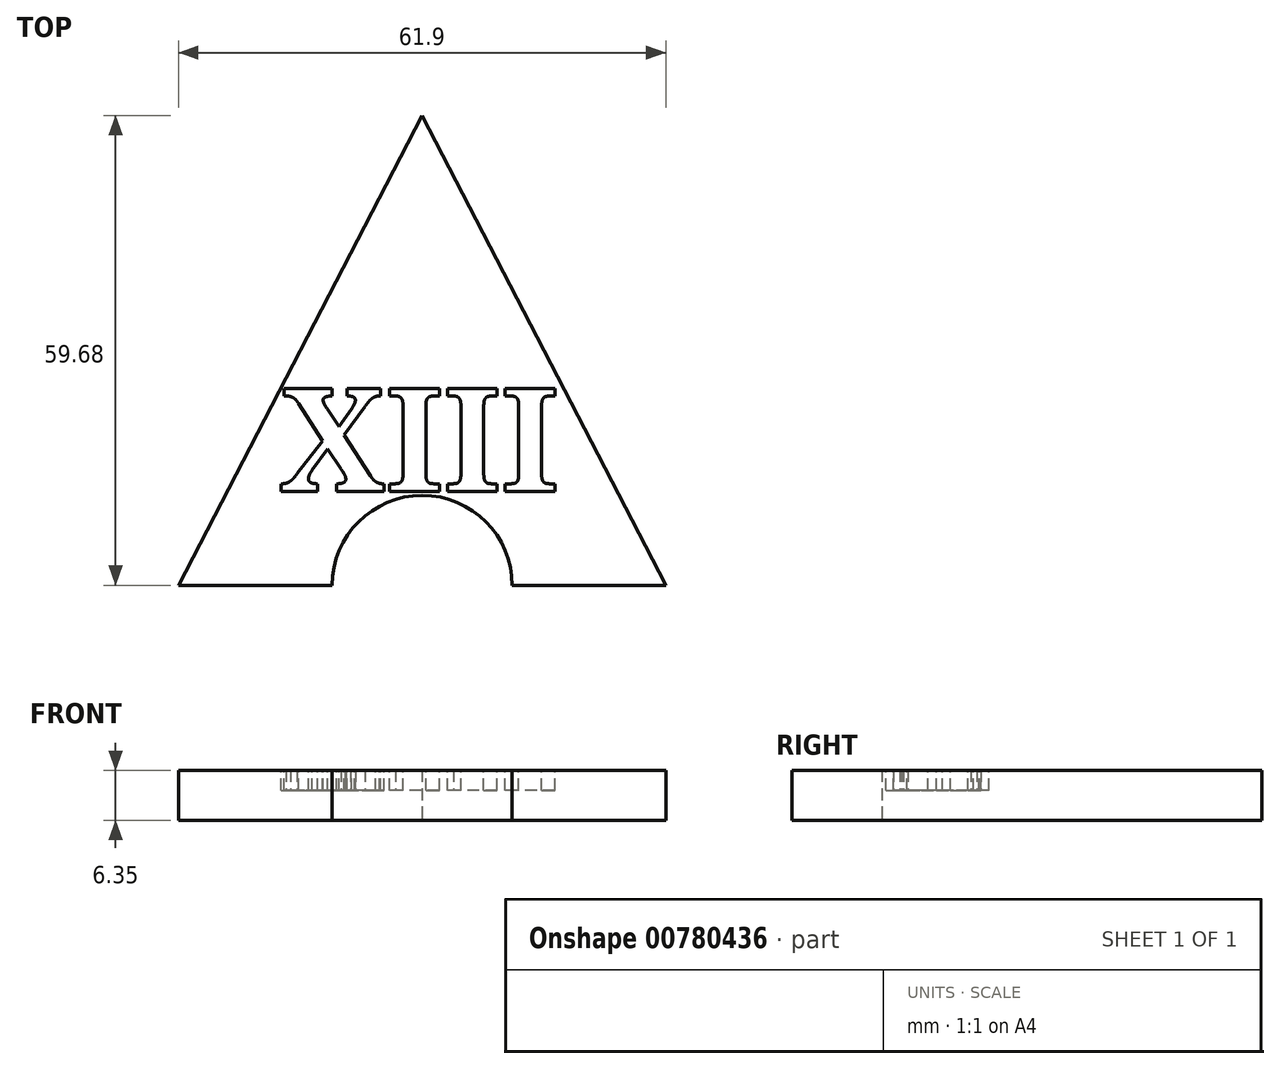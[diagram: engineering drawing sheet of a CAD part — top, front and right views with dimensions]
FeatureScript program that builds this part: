
annotation { "Feature Type Name" : "Feature", "Feature Type Description" : "" }
export const myFeature = defineFeature(function(context is Context, id is Id, definition is map)
    precondition{}
    {
        {
            var Q0;
            Q0=qCreatedBy(makeId("Top.planeOp"),FACE);
            var sketch = newSketch(context, id + "F0", { "sketchPlane" : qUnion([Q0])});
            skCircle(sketch, "E0.cCircle", {"center": v(0, -1.66) * mm, "radius": 17.87 * mm, "construction": true});
            skLineSegment(sketch, "E0.0", {"start": v(30.95, -19.52) * mm, "end": v(-30.95, -19.52) * mm});
            skLineSegment(sketch, "E0.1", {"start": v(-30.95, -19.52) * mm, "end": v(0, 40.16) * mm});
            skLineSegment(sketch, "E0.2", {"start": v(0, 40.16) * mm, "end": v(30.95, -19.52) * mm});
            skPoint(sketch, "E0.0.midPoint", {"position": v(0, -19.52) * mm});
            skSolve(sketch);
        }
        {
            var Q0;
            Q0=makeQuery(id+"F0.imprint","IMPRINT",FACE,{"disambiguationData":[TD([[makeQuery(id+"F0.imprint","IMPRINT",EDGE,{"derivedFrom":sQuery(id+"F0.wireOp",EDGE,"E0.0")}),-1.0]])]});
            extrude(context, id + "F1", {"entities" : qUnion([Q0]), "depth" : 6.35 * mm, "offsetDistance" : 25.4 * mm});
        }
        {
            var Q0;
            Q0=sQuery(id+"F0.wireOp",VERTEX,"E0.0.midPoint");
            var Q1;
            Q1=makeQuery(id+"F1.opExtrude","SWEPT_BODY",BODY,{"disambiguationData":[OSD([sQuery(id+"F0.wireOp",EDGE,"E0.0"),sQuery(id+"F0.wireOp",EDGE,"E0.1"),sQuery(id+"F0.wireOp",EDGE,"E0.2")])]});
            hole(context, id + "F2", {"style" : HoleStyle.SIMPLE, "endStyle" : HoleEndStyle.THROUGH, "oppositeDirection" : true, "holeDiameter" : 22.86 * mm, "majorDiameter" : 6.35 * mm, "isTappedThrough" : true, "tappedDepth" : 12.7 * mm, "tapClearance" : 3, "locations" : qUnion([Q0]), "scope" : qUnion([Q1])});
        }
        {
            var Q0;
            Q0=makeQuery(id+"F1.opExtrude","CAP_FACE",FACE,{"disambiguationData":[OSD([sQuery(id+"F0.wireOp",EDGE,"E0.0"),sQuery(id+"F0.wireOp",EDGE,"E0.1"),sQuery(id+"F0.wireOp",EDGE,"E0.2")])],"isStart":false});
            var sketch = newSketch(context, id + "F3", { "sketchPlane" : qUnion([Q0])});
            skText(sketch, "E1", { "text": "XIII", "fontName": "NotoSerif-Bold.ttf"});
            const initialGuessF3  = {"E1": [-0.01808, -0.00759, 1, 0, 0.0132]};
            skSetInitialGuess(sketch, initialGuessF3);
            skSolve(sketch);
        }
        {
            var Q0;
            Q0 = qSketchRegion(id + "F3", true);
            extrude(context, id + "F4", {"entities" : qUnion([Q0]), "operationType" : NewBodyOperationType.REMOVE, "oppositeDirection" : true, "depth" : 2.54 * mm, "offsetDistance" : 25.4 * mm});
        }
    });
